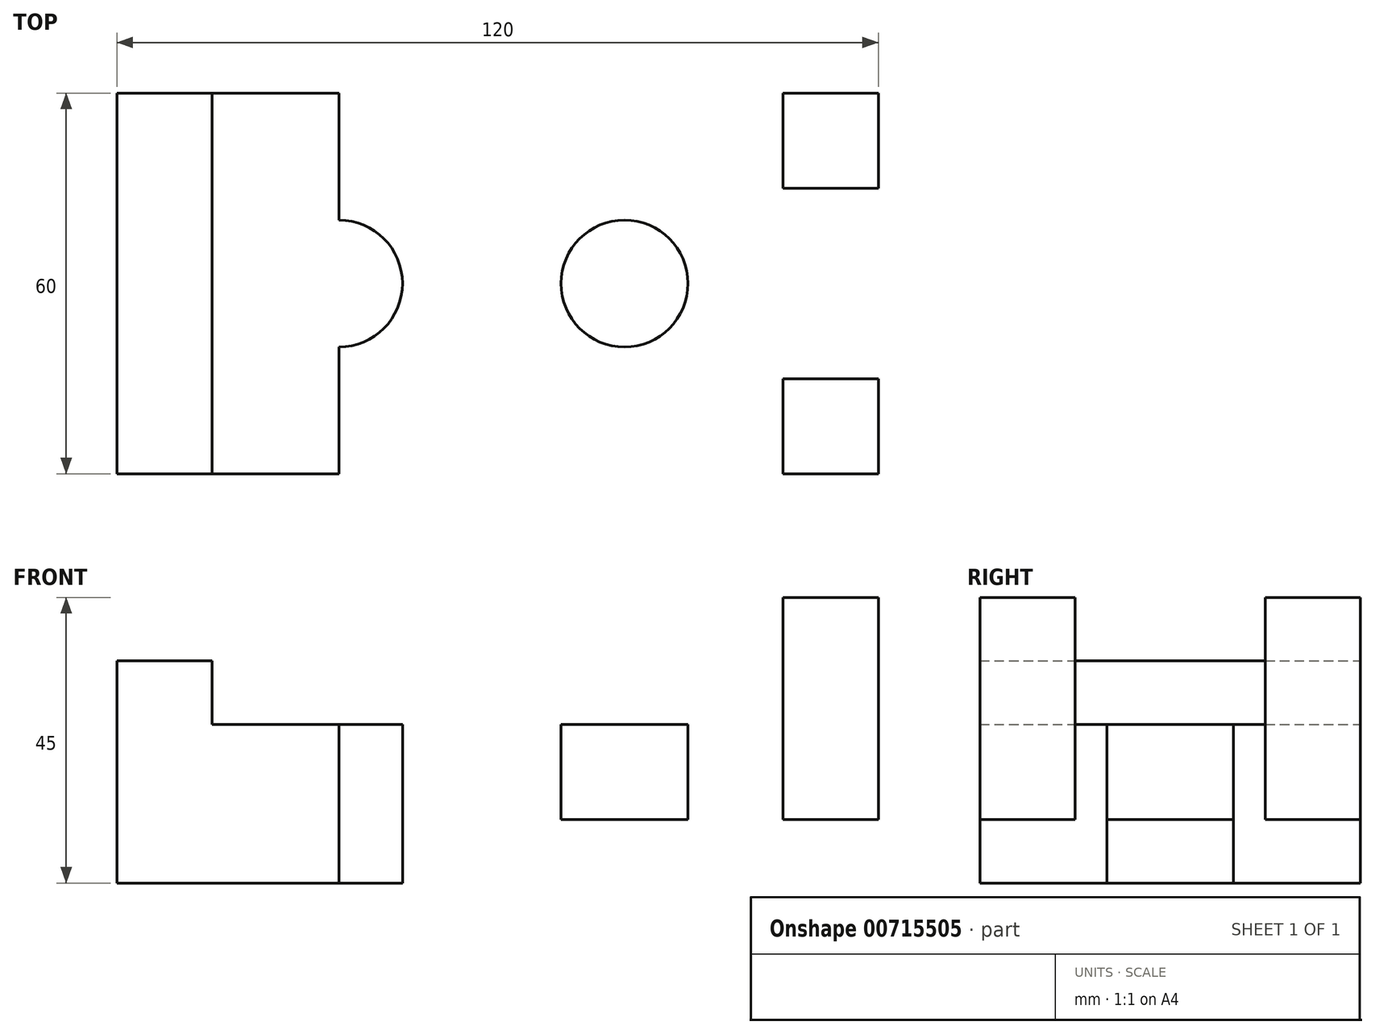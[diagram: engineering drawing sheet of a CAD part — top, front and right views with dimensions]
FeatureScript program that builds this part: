
annotation { "Feature Type Name" : "Feature", "Feature Type Description" : "" }
export const myFeature = defineFeature(function(context is Context, id is Id, definition is map)
    precondition{}
    {
        {
            var Q0;
            Q0=qCreatedBy(makeId("Top.planeOp"),FACE);
            var sketch = newSketch(context, id + "F0", { "sketchPlane" : qUnion([Q0])});
            skLineSegment(sketch, "E0.bottom", {"start": v(60, 30) * mm, "end": v(-60, 30) * mm});
            skLineSegment(sketch, "E0.top", {"start": v(60, -30) * mm, "end": v(-60, -30) * mm});
            skLineSegment(sketch, "E0.left", {"start": v(60, 30) * mm, "end": v(60, -30) * mm});
            skLineSegment(sketch, "E0.right", {"start": v(-60, 30) * mm, "end": v(-60, -30) * mm});
            skPoint(sketch, "E0.middle", {"position": v(0, 0) * mm});
            skSolve(sketch);
        }
        {
            var Q0;
            Q0=makeQuery(id+"F0.imprint","IMPRINT",FACE,{"disambiguationData":[TD([[makeQuery(id+"F0.imprint","IMPRINT",EDGE,{"derivedFrom":sQuery(id+"F0.wireOp",EDGE,"E0.bottom")}),1.0]])]});
            extrude(context, id + "F1", {"entities" : qUnion([Q0]), "depth" : 25 * mm, "offsetDistance" : 25 * mm});
        }
        {
            var Q0;
            Q0=makeQuery(id+"F1.opExtrude","CAP_FACE",FACE,{"disambiguationData":[OSD([sQuery(id+"F0.wireOp",EDGE,"E0.bottom"),sQuery(id+"F0.wireOp",EDGE,"E0.top"),sQuery(id+"F0.wireOp",EDGE,"E0.left"),sQuery(id+"F0.wireOp",EDGE,"E0.right")])],"isStart":true});
            var sketch = newSketch(context, id + "F2", { "sketchPlane" : qUnion([Q0])});
            skLineSegment(sketch, "E1.bottom", {"start": v(60, 30) * mm, "end": v(0, 30) * mm});
            skLineSegment(sketch, "E1.top", {"start": v(60, -30) * mm, "end": v(0, -30) * mm});
            skLineSegment(sketch, "E1.left", {"start": v(60, 30) * mm, "end": v(60, -30) * mm});
            skLineSegment(sketch, "E1.right", {"start": v(0, 30) * mm, "end": v(0, -30) * mm});
            skSolve(sketch);
        }
        {
            var Q0;
            Q0 = qSketchRegion(id + "F2", true);
            extrude(context, id + "F3", {"entities" : qUnion([Q0]), "operationType" : NewBodyOperationType.REMOVE, "oppositeDirection" : true, "depth" : 10 * mm, "offsetDistance" : 25 * mm});
        }
        {
            var Q0;
            Q0=makeQuery(id+"F1.opExtrude","CAP_FACE",FACE,{"disambiguationData":[OSD([sQuery(id+"F0.wireOp",EDGE,"E0.bottom"),sQuery(id+"F0.wireOp",EDGE,"E0.top"),sQuery(id+"F0.wireOp",EDGE,"E0.left"),sQuery(id+"F0.wireOp",EDGE,"E0.right")])],"isStart":false});
            var sketch = newSketch(context, id + "F4", { "sketchPlane" : qUnion([Q0])});
            skLineSegment(sketch, "E2.bottom", {"start": v(-60, -30) * mm, "end": v(-45, -30) * mm});
            skLineSegment(sketch, "E2.top", {"start": v(-60, 30) * mm, "end": v(-45, 30) * mm});
            skLineSegment(sketch, "E2.left", {"start": v(-60, -30) * mm, "end": v(-60, 30) * mm});
            skLineSegment(sketch, "E2.right", {"start": v(-45, -30) * mm, "end": v(-45, 30) * mm});
            skSolve(sketch);
        }
        {
            var Q0;
            Q0 = qSketchRegion(id + "F4", true);
            extrude(context, id + "F5", {"entities" : qUnion([Q0]), "operationType" : NewBodyOperationType.ADD, "depth" : 10 * mm, "offsetDistance" : 25 * mm});
        }
        {
            var Q0;
            Q0=makeQuery(id+"F1.opExtrude","CAP_FACE",FACE,{"disambiguationData":[OSD([sQuery(id+"F0.wireOp",EDGE,"E0.bottom"),sQuery(id+"F0.wireOp",EDGE,"E0.top"),sQuery(id+"F0.wireOp",EDGE,"E0.left"),sQuery(id+"F0.wireOp",EDGE,"E0.right")])],"isStart":false});
            var sketch = newSketch(context, id + "F6", { "sketchPlane" : qUnion([Q0])});
            skLineSegment(sketch, "E3.bottom", {"start": v(60, -30) * mm, "end": v(45, -30) * mm});
            skLineSegment(sketch, "E3.top", {"start": v(60, -15) * mm, "end": v(45, -15) * mm});
            skLineSegment(sketch, "E3.left", {"start": v(60, -30) * mm, "end": v(60, -15) * mm});
            skLineSegment(sketch, "E3.right", {"start": v(45, -30) * mm, "end": v(45, -15) * mm});
            skLineSegment(sketch, "E4.bottom", {"start": v(60, 30) * mm, "end": v(45, 30) * mm});
            skLineSegment(sketch, "E4.top", {"start": v(60, 15) * mm, "end": v(45, 15) * mm});
            skLineSegment(sketch, "E4.left", {"start": v(60, 30) * mm, "end": v(60, 15) * mm});
            skLineSegment(sketch, "E4.right", {"start": v(45, 30) * mm, "end": v(45, 15) * mm});
            skSolve(sketch);
        }
        {
            var Q0;
            Q0 = qSketchRegion(id + "F6", true);
            extrude(context, id + "F7", {"entities" : qUnion([Q0]), "operationType" : NewBodyOperationType.ADD, "depth" : 20 * mm, "offsetDistance" : 25 * mm});
        }
        {
            var Q0;
            Q0=makeQuery(id+"F1.opExtrude","CAP_FACE",FACE,{"disambiguationData":[OSD([sQuery(id+"F0.wireOp",EDGE,"E0.bottom"),sQuery(id+"F0.wireOp",EDGE,"E0.top"),sQuery(id+"F0.wireOp",EDGE,"E0.left"),sQuery(id+"F0.wireOp",EDGE,"E0.right")])],"isStart":false});
            var sketch = newSketch(context, id + "F8", { "sketchPlane" : qUnion([Q0])});
            skLineSegment(sketch, "E5.bottom", {"start": v(-45, -30) * mm, "end": v(-25, -30) * mm});
            skLineSegment(sketch, "E5.top", {"start": v(-45, 30) * mm, "end": v(-25, 30) * mm});
            skLineSegment(sketch, "E5.left", {"start": v(-45, -30) * mm, "end": v(-45, 30) * mm});
            skLineSegment(sketch, "E5.right", {"start": v(-25, -30) * mm, "end": v(-25, 30) * mm});
            skLineSegment(sketch, "E6.bottom", {"start": v(-25, 30) * mm, "end": v(20, 30) * mm});
            skLineSegment(sketch, "E6.top", {"start": v(-25, -30) * mm, "end": v(20, -30) * mm});
            skLineSegment(sketch, "E6.left", {"start": v(-25, 30) * mm, "end": v(-25, -30) * mm});
            skLineSegment(sketch, "E6.right", {"start": v(20, 30) * mm, "end": v(20, -30) * mm});
            skCircle(sketch, "E7", {"center": v(-25, 0) * mm, "radius": 10 * mm});
            skCircle(sketch, "E8", {"center": v(20, 0) * mm, "radius": 10 * mm});
            skSolve(sketch);
        }
        {
            var Q0;
            {var subQ0=sQuery(id+"F8.wireOp",EDGE,"E7");var subQ1=sQuery(id+"F8.wireOp",EDGE,"E6.left");var subQ2=makeQuery(id+"F8.imprint","INTERSECT",VERTEX,{"disambiguationData":[OD(0.0)],"derivedFrom":[subQ1,subQ0]});Q0=makeQuery(id+"F8.imprint","IMPRINT",FACE,{"disambiguationData":[TD([[makeQuery(id+"F8.imprint","IMPRINT",EDGE,{"disambiguationData":[TD([[subQ2,-1.0]])],"derivedFrom":subQ1}),-1.0]])]});}
            var Q1;
            {var subQ0=sQuery(id+"F8.wireOp",EDGE,"E7");var subQ1=sQuery(id+"F8.wireOp",EDGE,"E6.left");var subQ2=makeQuery(id+"F8.imprint","INTERSECT",VERTEX,{"disambiguationData":[OD(0.0)],"derivedFrom":[subQ1,subQ0]});Q1=makeQuery(id+"F8.imprint","IMPRINT",FACE,{"disambiguationData":[TD([[makeQuery(id+"F8.imprint","IMPRINT",EDGE,{"disambiguationData":[TD([[subQ2,-1.0]])],"derivedFrom":subQ1}),1.0]])]});}
            var Q2;
            {var subQ0=sQuery(id+"F8.wireOp",EDGE,"E8");var subQ1=sQuery(id+"F8.wireOp",EDGE,"E6.right");var subQ2=makeQuery(id+"F8.imprint","INTERSECT",VERTEX,{"disambiguationData":[OD(0.0)],"derivedFrom":[subQ1,subQ0]});Q2=makeQuery(id+"F8.imprint","IMPRINT",FACE,{"disambiguationData":[TD([[makeQuery(id+"F8.imprint","IMPRINT",EDGE,{"disambiguationData":[TD([[subQ2,-1.0]])],"derivedFrom":subQ1}),-1.0]])]});}
            var Q3;
            {var subQ0=sQuery(id+"F8.wireOp",EDGE,"E8");var subQ1=sQuery(id+"F8.wireOp",EDGE,"E6.right");var subQ2=makeQuery(id+"F8.imprint","INTERSECT",VERTEX,{"disambiguationData":[OD(0.0)],"derivedFrom":[subQ1,subQ0]});Q3=makeQuery(id+"F8.imprint","IMPRINT",FACE,{"disambiguationData":[TD([[makeQuery(id+"F8.imprint","IMPRINT",EDGE,{"disambiguationData":[TD([[subQ2,-1.0]])],"derivedFrom":subQ1}),1.0]])]});}
            extrude(context, id + "F9", {"entities" : qUnion([Q0, Q1, Q2, Q3]), "operationType" : NewBodyOperationType.REMOVE, "endBound" : BoundingType.THROUGH_ALL, "oppositeDirection" : true, "depth" : 25 * mm, "offsetDistance" : 25 * mm});
        }
    });
